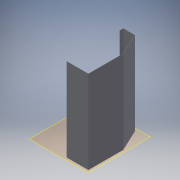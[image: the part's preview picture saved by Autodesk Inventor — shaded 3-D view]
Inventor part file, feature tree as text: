
AUTODESK INVENTOR PART (.ipt)
format: ipt  version: 2018 (Build 220112000, 112)  size: 127,488 bytes
history: native  units: mm
features: reference x5, other x3, plane x2, extrude x2, sketch x2, mirror x1
ambient origin geometry x8: Origin, YZ Plane, XZ Plane, XY Plane, X Axis, Y Axis, Z Axis, Center Point
bodies: Solid1 (feature_tree)
feature tree (15):
  plane  "Work Plane1"
  extrude  "Extrusion1"  Depth=1.6mm
  extrude  "Extrusion2"  Depth=816.6mm
  plane  "Work Plane2"
  mirror  "Mirror1"
  sketch  "Sketch1"  dims[d0=50.0mm d1=1.6mm]
  reference  "Reference1"
  reference  "Reference2"
  reference  "Reference3"
  reference  "Reference4"
  sketch  "Sketch2"  dims[d2=1.6mm d3=816.6mm d4=816.6mm d5=1198.4mm d6=0.0mm d8=1.6mm d9=0.0mm d10=1.6mm d11=0.0mm d14=1.6mm]
  reference  "Reference5"
  other  "Lathe Model 2018.iam"
  other  "Cover V3-01:a"
  other  "Cover V3:1"
